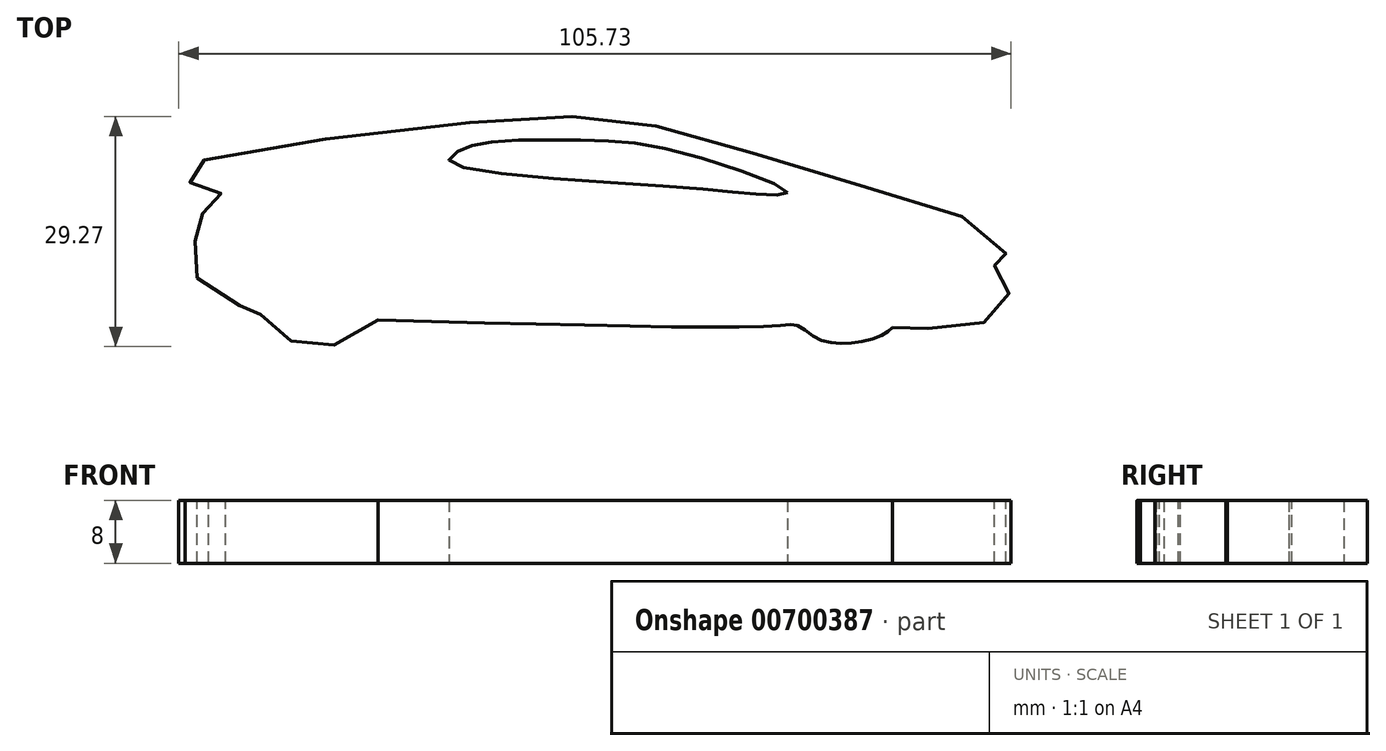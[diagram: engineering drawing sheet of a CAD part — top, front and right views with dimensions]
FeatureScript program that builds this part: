
annotation { "Feature Type Name" : "Feature", "Feature Type Description" : "" }
export const myFeature = defineFeature(function(context is Context, id is Id, definition is map)
    precondition{}
    {
        {
            var Q0;
            Q0=qCreatedBy(makeId("Top.planeOp"),FACE);
            var sketch = newSketch(context, id + "F0", { "sketchPlane" : qUnion([Q0])});
            skFitSpline(sketch, "E0", {"points": [v(0, -65.9) * mm, v(50.85, -66.63) * mm, v(53.3, -66.63) * mm, v(55.51, -68.1) * mm, v(58.21, -68.84) * mm, v(61.65, -68.6) * mm, v(64.35, -67.62) * mm, v(65.33, -66.88) * mm], "startDerivative": vector(157.22, -4.27) * mm, "endDerivative": vector(12.53, 11.07) * mm});
            skFitSpline(sketch, "E1", {"points": [v(65.33, -66.88) * mm, v(68.03, -66.88) * mm, v(73.67, -66.88) * mm, v(80.3, -64.18) * mm, v(79.32, -61.23) * mm, v(78.34, -59.52) * mm, v(78.83, -57.8) * mm, v(79.56, -58.04) * mm, v(79.07, -55.84) * mm, v(59.2, -48.23) * mm, v(33.18, -40.86) * mm, v(11.09, -40.86) * mm, v(-24.99, -46.75) * mm, v(-24.74, -47.98) * mm, v(-19.34, -49.94) * mm, v(-22.78, -49.94) * mm, v(-21.55, -54.36) * mm, v(-22.78, -55.59) * mm, v(-24.5, -57.8) * mm, v(-19.1, -63.69) * mm, v(-16.9, -63.93) * mm, v(-15.9, -63.93) * mm, v(-13.7, -66.88) * mm, v(-10.26, -68.84) * mm, v(-5.6, -69.09) * mm, v(0, -65.9) * mm], "startDerivative": vector(90.18, 2.45) * mm, "endDerivative": vector(128.63, 94.02) * mm});
            skFitSpline(sketch, "E2", {"points": [v(52.02, -49.7) * mm, v(49.08, -49.94) * mm, v(37.05, -48.96) * mm, v(9.07, -45.77) * mm, v(10.05, -44.55) * mm, v(14.23, -43.32) * mm, v(26.5, -43.07) * mm, v(38.28, -44.55) * mm, v(52.02, -49.7) * mm]});
            skSolve(sketch);
        }
        {
            var Q0;
            Q0 = qSketchRegion(id + "F0", true);
            var Q1;
            Q1=sQuery(id+"F0.wireOp",EDGE,"E1");
            var Q2;
            Q2=sQuery(id+"F0.wireOp",EDGE,"E0");
            var Q3;
            Q3=sQuery(id+"F0.wireOp",EDGE,"E2");
            extrude(context, id + "F1", {"entities" : qUnion([Q0]), "bodyType" : ToolBodyType.SURFACE, "operationType" : NewBodyOperationType.INTERSECT, "surfaceEntities" : qUnion([Q1, Q2, Q3]), "oppositeDirection" : true, "depth" : 8 * mm, "offsetDistance" : 25.4 * mm});
        }
    });
